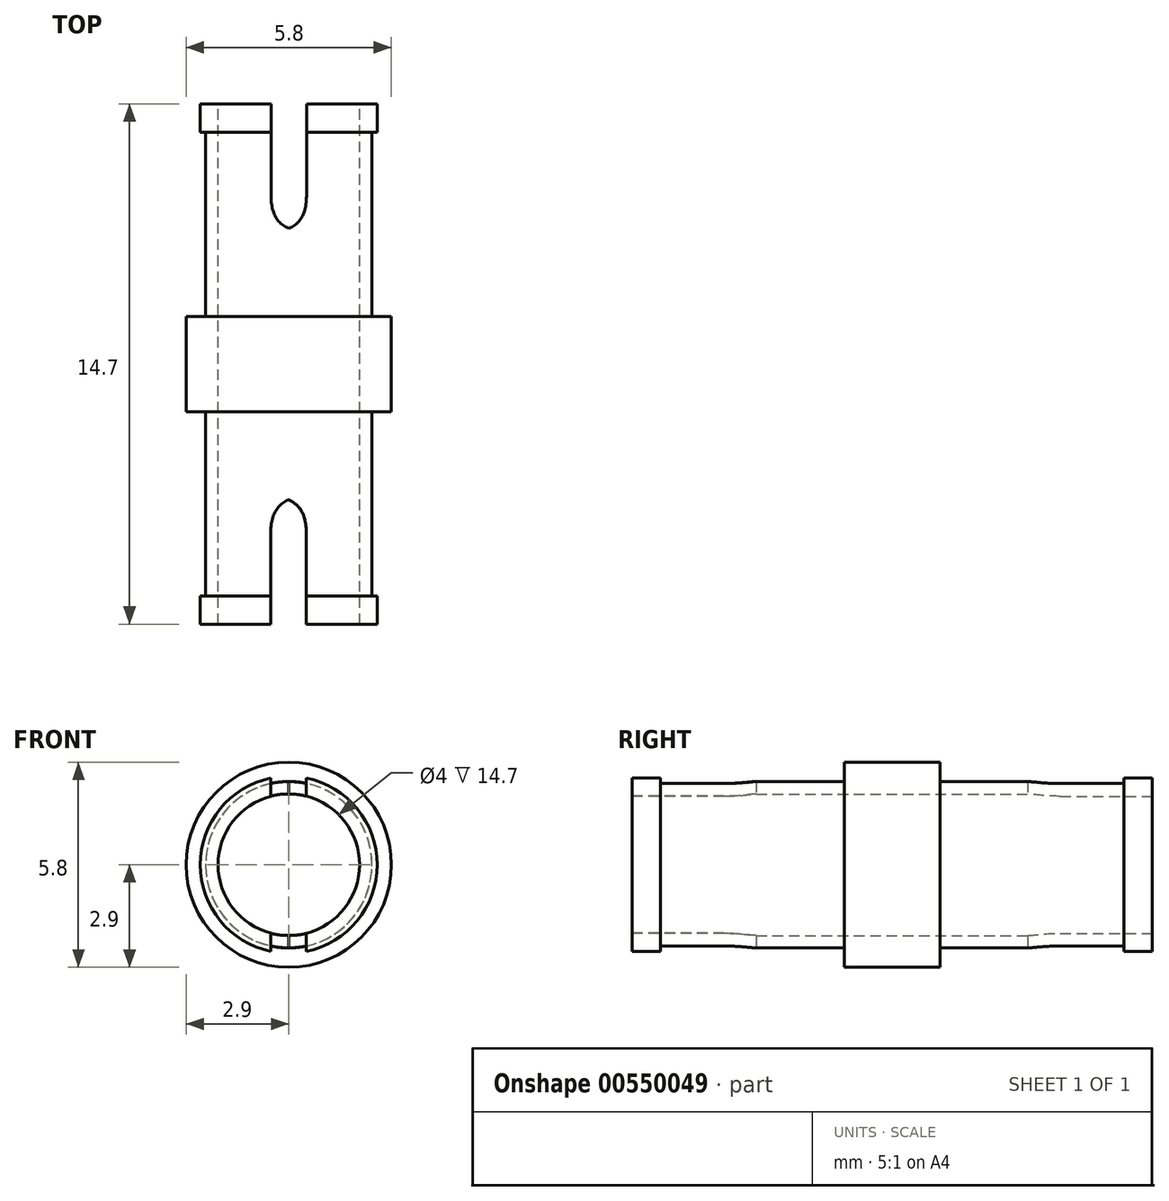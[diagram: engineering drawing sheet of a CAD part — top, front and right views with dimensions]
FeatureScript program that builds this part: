
annotation { "Feature Type Name" : "Feature", "Feature Type Description" : "" }
export const myFeature = defineFeature(function(context is Context, id is Id, definition is map)
    precondition{}
    {
        {
            var Q0;
            Q0=qCreatedBy(makeId("Front.planeOp"),FACE);
            var sketch = newSketch(context, id + "F0", { "sketchPlane" : qUnion([Q0])});
            skCircle(sketch, "E0", {"center": v(0, 0) * mm, "radius": 2.9 * mm});
            skCircle(sketch, "E1", {"center": v(0, 0) * mm, "radius": 2.35 * mm});
            skSolve(sketch);
        }
        {
            var Q0;
            Q0=makeQuery(id+"F0.imprint","IMPRINT",FACE,{"disambiguationData":[TD([[makeQuery(id+"F0.imprint","IMPRINT",EDGE,{"derivedFrom":sQuery(id+"F0.wireOp",EDGE,"E0")}),1.0]])]});
            var Q1;
            Q1=makeQuery(id+"F0.imprint","IMPRINT",FACE,{"disambiguationData":[TD([[makeQuery(id+"F0.imprint","IMPRINT",EDGE,{"derivedFrom":sQuery(id+"F0.wireOp",EDGE,"E1")}),1.0]])]});
            extrude(context, id + "F1", {"entities" : qUnion([Q0, Q1]), "depth" : 2.7 * mm, "offsetDistance" : 25 * mm});
        }
        {
            var Q0;
            Q0=makeQuery(id+"F0.imprint","IMPRINT",FACE,{"disambiguationData":[TD([[makeQuery(id+"F0.imprint","IMPRINT",EDGE,{"derivedFrom":sQuery(id+"F0.wireOp",EDGE,"E1")}),1.0]])]});
            var Q1;
            Q1=sQuery(id+"F0.wireOp",EDGE,"E1");
            extrude(context, id + "F2", {"entities" : qUnion([Q0]), "operationType" : NewBodyOperationType.ADD, "surfaceEntities" : qUnion([Q1]), "oppositeDirection" : true, "depth" : 6 * mm, "offsetDistance" : 25 * mm});
        }
        {
            var Q0;
            Q0=makeQuery(id+"F1.opExtrude","CAP_FACE",FACE,{"disambiguationData":[OSD([sQuery(id+"F0.wireOp",EDGE,"E0")])],"isStart":false});
            var sketch = newSketch(context, id + "F3", { "sketchPlane" : qUnion([Q0])});
            skCircle(sketch, "E2", {"center": v(0, 0) * mm, "radius": 2.35 * mm});
            skSolve(sketch);
        }
        {
            var Q0;
            Q0=makeQuery(id+"F3.imprint","IMPRINT",FACE,{"disambiguationData":[TD([[makeQuery(id+"F3.imprint","IMPRINT",EDGE,{"derivedFrom":sQuery(id+"F3.wireOp",EDGE,"E2")}),1.0]])]});
            var Q1;
            Q1=sQuery(id+"F3.wireOp",EDGE,"E2");
            extrude(context, id + "F4", {"entities" : qUnion([Q0]), "operationType" : NewBodyOperationType.ADD, "surfaceEntities" : qUnion([Q1]), "depth" : 6 * mm, "offsetDistance" : 25 * mm});
        }
        {
            var Q0;
            Q0=makeQuery(id+"F2.opExtrude","CAP_FACE",FACE,{"disambiguationData":[OSD([sQuery(id+"F0.wireOp",EDGE,"E1")])],"isStart":false});
            var sketch = newSketch(context, id + "F5", { "sketchPlane" : qUnion([Q0])});
            skCircle(sketch, "E3", {"center": v(0, 0) * mm, "radius": 2.5 * mm});
            skSolve(sketch);
        }
        {
            var Q0;
            Q0=makeQuery(id+"F5.imprint","IMPRINT",FACE,{"disambiguationData":[TD([[makeQuery(id+"F5.imprint","IMPRINT",EDGE,{"derivedFrom":sQuery(id+"F5.wireOp",EDGE,"E3")}),1.0]])]});
            var Q1;
            Q1=sQuery(id+"F5.wireOp",EDGE,"E3");
            extrude(context, id + "F6", {"entities" : qUnion([Q0]), "operationType" : NewBodyOperationType.ADD, "surfaceEntities" : qUnion([Q1]), "oppositeDirection" : true, "depth" : 0.8 * mm, "offsetDistance" : 25 * mm});
        }
        {
            var Q0;
            Q0=makeQuery(id+"F4.opExtrude","CAP_FACE",FACE,{"disambiguationData":[OSD([sQuery(id+"F3.wireOp",EDGE,"E2")])],"isStart":false});
            var sketch = newSketch(context, id + "F7", { "sketchPlane" : qUnion([Q0])});
            skCircle(sketch, "E4", {"center": v(0, 0) * mm, "radius": 2.5 * mm});
            skSolve(sketch);
        }
        {
            var Q0;
            Q0=makeQuery(id+"F7.imprint","IMPRINT",FACE,{"disambiguationData":[TD([[makeQuery(id+"F7.imprint","IMPRINT",EDGE,{"derivedFrom":sQuery(id+"F7.wireOp",EDGE,"E4")}),1.0]])]});
            var Q1;
            Q1=sQuery(id+"F7.wireOp",EDGE,"E4");
            extrude(context, id + "F8", {"entities" : qUnion([Q0]), "operationType" : NewBodyOperationType.ADD, "surfaceEntities" : qUnion([Q1]), "oppositeDirection" : true, "depth" : 0.8 * mm, "offsetDistance" : 25 * mm});
        }
        {
            var Q0;
            {var subQ0=sQuery(id+"F0.wireOp",EDGE,"E1");Q0=makeQuery(id+"F6.boolean.opBoolean","MERGE",FACE,{"derivedFrom":[makeQuery(id+"F2.opExtrude","CAP_FACE",FACE,{"disambiguationData":[OSD([subQ0])],"isStart":false}),makeQuery(id+"F6.opExtrude","CAP_FACE",FACE,{"disambiguationData":[OSD([subQ0,sQuery(id+"F5.wireOp",EDGE,"E3")])],"isStart":true})]});}
            var sketch = newSketch(context, id + "F9", { "sketchPlane" : qUnion([Q0])});
            skCircle(sketch, "E5", {"center": v(0, 0) * mm, "radius": 2 * mm});
            skSolve(sketch);
        }
        {
            var Q0;
            Q0=makeQuery(id+"F9.imprint","IMPRINT",FACE,{"disambiguationData":[TD([[makeQuery(id+"F9.imprint","IMPRINT",EDGE,{"derivedFrom":sQuery(id+"F9.wireOp",EDGE,"E5")}),1.0]])]});
            var Q1;
            {var subQ0=sQuery(id+"F3.wireOp",EDGE,"E2");Q1=makeQuery(id+"F8.boolean.opBoolean","MERGE",FACE,{"derivedFrom":[makeQuery(id+"F4.opExtrude","CAP_FACE",FACE,{"disambiguationData":[OSD([subQ0])],"isStart":false}),makeQuery(id+"F8.opExtrude","CAP_FACE",FACE,{"disambiguationData":[OSD([subQ0,sQuery(id+"F7.wireOp",EDGE,"E4")])],"isStart":true})]});}
            extrude(context, id + "F10", {"entities" : qUnion([Q0]), "operationType" : NewBodyOperationType.REMOVE, "endBound" : BoundingType.UP_TO_SURFACE, "oppositeDirection" : true, "depth" : 25 * mm, "endBoundEntityFace" : qUnion([Q1]), "offsetDistance" : 25 * mm});
        }
        {
            var Q0;
            {var subQ0=sQuery(id+"F0.wireOp",EDGE,"E1");Q0=makeQuery(id+"F6.boolean.opBoolean","MERGE",FACE,{"derivedFrom":[makeQuery(id+"F2.opExtrude","CAP_FACE",FACE,{"disambiguationData":[OSD([subQ0])],"isStart":false}),makeQuery(id+"F6.opExtrude","CAP_FACE",FACE,{"disambiguationData":[OSD([subQ0,sQuery(id+"F5.wireOp",EDGE,"E3")])],"isStart":true})]});}
            var sketch = newSketch(context, id + "F11", { "sketchPlane" : qUnion([Q0])});
            skLineSegment(sketch, "E6", {"start": v(0.5, 2) * mm, "end": v(0.5, 2.54) * mm});
            skLineSegment(sketch, "E7", {"start": v(0.5, 2.54) * mm, "end": v(-0.5, 2.54) * mm});
            skLineSegment(sketch, "E8", {"start": v(-0.5, 2.54) * mm, "end": v(-0.5, 2) * mm});
            skLineSegment(sketch, "E9", {"start": v(-0.5, 1.82) * mm, "end": v(0.5, 1.82) * mm});
            skLineSegment(sketch, "E10", {"start": v(0.5, 1.82) * mm, "end": v(0.5, 2) * mm});
            skLineSegment(sketch, "E11", {"start": v(-0.5, 2) * mm, "end": v(-0.5, 1.82) * mm});
            skLineSegment(sketch, "E12", {"start": v(-2.5, 0) * mm, "end": v(2.5, 0) * mm});
            skLineSegment(sketch, "E13.MirrorCS", {"start": v(0.5, -2.54) * mm, "end": v(-0.5, -2.54) * mm});
            skLineSegment(sketch, "E14.MirrorCS", {"start": v(0.5, -2) * mm, "end": v(0.5, -2.54) * mm});
            skLineSegment(sketch, "E15.MirrorCS", {"start": v(-0.5, -2.54) * mm, "end": v(-0.5, -2) * mm});
            skLineSegment(sketch, "E16.MirrorCS", {"start": v(-0.5, -1.82) * mm, "end": v(0.5, -1.82) * mm});
            skLineSegment(sketch, "E17.MirrorCS", {"start": v(0.5, -1.82) * mm, "end": v(0.5, -2) * mm});
            skLineSegment(sketch, "E18.MirrorCS", {"start": v(-0.5, -2) * mm, "end": v(-0.5, -1.82) * mm});
            skSolve(sketch);
        }
        {
            var Q0;
            {var subQ0=sQuery(id+"F3.wireOp",EDGE,"E2");Q0=makeQuery(id+"F8.boolean.opBoolean","MERGE",FACE,{"derivedFrom":[makeQuery(id+"F4.opExtrude","CAP_FACE",FACE,{"disambiguationData":[OSD([subQ0])],"isStart":false}),makeQuery(id+"F8.opExtrude","CAP_FACE",FACE,{"disambiguationData":[OSD([subQ0,sQuery(id+"F7.wireOp",EDGE,"E4")])],"isStart":true})]});}
            var sketch = newSketch(context, id + "F12", { "sketchPlane" : qUnion([Q0])});
            skLineSegment(sketch, "E19", {"start": v(0.5, 2) * mm, "end": v(0.5, 2.54) * mm});
            skLineSegment(sketch, "E20", {"start": v(0.5, 2.54) * mm, "end": v(-0.5, 2.54) * mm});
            skLineSegment(sketch, "E21", {"start": v(-0.5, 2.54) * mm, "end": v(-0.5, 2) * mm});
            skLineSegment(sketch, "E22", {"start": v(-0.5, 1.83) * mm, "end": v(0.5, 1.83) * mm});
            skLineSegment(sketch, "E23", {"start": v(0.5, 1.83) * mm, "end": v(0.5, 2) * mm});
            skLineSegment(sketch, "E24", {"start": v(-0.5, 2) * mm, "end": v(-0.5, 1.83) * mm});
            skLineSegment(sketch, "E25", {"start": v(-2.5, 0) * mm, "end": v(2.5, 0) * mm});
            skLineSegment(sketch, "E26.MirrorCS", {"start": v(0.5, -2.53) * mm, "end": v(-0.5, -2.53) * mm});
            skLineSegment(sketch, "E27.MirrorCS", {"start": v(0.5, -2) * mm, "end": v(0.5, -2.53) * mm});
            skLineSegment(sketch, "E28.MirrorCS", {"start": v(-0.5, -2.53) * mm, "end": v(-0.5, -2) * mm});
            skLineSegment(sketch, "E29.MirrorCS", {"start": v(-0.5, -1.81) * mm, "end": v(0.5, -1.81) * mm});
            skLineSegment(sketch, "E30.MirrorCS", {"start": v(0.5, -1.81) * mm, "end": v(0.5, -2) * mm});
            skLineSegment(sketch, "E31.MirrorCS", {"start": v(-0.5, -2) * mm, "end": v(-0.5, -1.81) * mm});
            skSolve(sketch);
        }
        {
            var Q0;
            {var subQ5=sQuery(id+"F11.wireOp",EDGE,"E10");var subQ6=sQuery(id+"F11.wireOp",EDGE,"E6");var subQ7=makeQuery(id+"F11.imprint","INTERSECT",VERTEX,{"derivedFrom":[subQ6,subQ5]});Q0=makeQuery(id+"F11.imprint","IMPRINT",FACE,{"disambiguationData":[TD([[makeQuery(id+"F11.imprint","IMPRINT",EDGE,{"disambiguationData":[TD([[subQ7,-1.0]])],"derivedFrom":subQ6}),1.0]])]});}
            var Q1;
            {var subQ5=sQuery(id+"F11.wireOp",EDGE,"E17.MirrorCS");var subQ6=sQuery(id+"F11.wireOp",EDGE,"E14.MirrorCS");var subQ7=makeQuery(id+"F11.imprint","INTERSECT",VERTEX,{"derivedFrom":[subQ6,subQ5]});Q1=makeQuery(id+"F11.imprint","IMPRINT",FACE,{"disambiguationData":[TD([[makeQuery(id+"F11.imprint","IMPRINT",EDGE,{"disambiguationData":[TD([[subQ7,-1.0]])],"derivedFrom":subQ6}),-1.0]])]});}
            extrude(context, id + "F13", {"entities" : qUnion([Q0, Q1]), "operationType" : NewBodyOperationType.REMOVE, "oppositeDirection" : true, "depth" : 3.6 * mm, "offsetDistance" : 25 * mm});
        }
        {
            var Q0;
            {var subQ7=sQuery(id+"F12.wireOp",EDGE,"E23");var subQ8=sQuery(id+"F12.wireOp",EDGE,"E19");var subQ9=makeQuery(id+"F12.imprint","INTERSECT",VERTEX,{"derivedFrom":[subQ8,subQ7]});Q0=makeQuery(id+"F12.imprint","IMPRINT",FACE,{"disambiguationData":[TD([[makeQuery(id+"F12.imprint","IMPRINT",EDGE,{"disambiguationData":[TD([[subQ9,-1.0]])],"derivedFrom":subQ8}),1.0]])]});}
            var Q1;
            {var subQ7=sQuery(id+"F12.wireOp",EDGE,"E30.MirrorCS");var subQ8=sQuery(id+"F12.wireOp",EDGE,"E27.MirrorCS");var subQ9=makeQuery(id+"F12.imprint","INTERSECT",VERTEX,{"derivedFrom":[subQ8,subQ7]});Q1=makeQuery(id+"F12.imprint","IMPRINT",FACE,{"disambiguationData":[TD([[makeQuery(id+"F12.imprint","IMPRINT",EDGE,{"disambiguationData":[TD([[subQ9,-1.0]])],"derivedFrom":subQ8}),-1.0]])]});}
            extrude(context, id + "F14", {"entities" : qUnion([Q0, Q1]), "operationType" : NewBodyOperationType.REMOVE, "oppositeDirection" : true, "depth" : 3.6 * mm, "offsetDistance" : 25 * mm});
        }
        {
            var Q0;
            Q0=makeQuery(id+"F14.boolean.opBoolean","COPY",EDGE,{"derivedFrom":makeQuery(id+"F14.opExtrude","CAP_EDGE",EDGE,{"disambiguationData":[OSD([sQuery(id+"F12.wireOp",EDGE,"E28.MirrorCS"),sQuery(id+"F12.wireOp",EDGE,"E31.MirrorCS")])],"isStart":false})});
            var Q1;
            Q1=makeQuery(id+"F14.boolean.opBoolean","COPY",EDGE,{"derivedFrom":makeQuery(id+"F14.opExtrude","CAP_EDGE",EDGE,{"disambiguationData":[OSD([sQuery(id+"F12.wireOp",EDGE,"E27.MirrorCS"),sQuery(id+"F12.wireOp",EDGE,"E30.MirrorCS")])],"isStart":false})});
            var Q2;
            Q2=makeQuery(id+"F14.boolean.opBoolean","COPY",EDGE,{"derivedFrom":makeQuery(id+"F14.opExtrude","CAP_EDGE",EDGE,{"disambiguationData":[OSD([sQuery(id+"F12.wireOp",EDGE,"E21"),sQuery(id+"F12.wireOp",EDGE,"E24")])],"isStart":false})});
            var Q3;
            Q3=makeQuery(id+"F14.boolean.opBoolean","COPY",EDGE,{"derivedFrom":makeQuery(id+"F14.opExtrude","CAP_EDGE",EDGE,{"disambiguationData":[OSD([sQuery(id+"F12.wireOp",EDGE,"E19"),sQuery(id+"F12.wireOp",EDGE,"E23")])],"isStart":false})});
            var Q4;
            Q4=makeQuery(id+"F13.boolean.opBoolean","COPY",EDGE,{"derivedFrom":makeQuery(id+"F13.opExtrude","CAP_EDGE",EDGE,{"disambiguationData":[OSD([sQuery(id+"F11.wireOp",EDGE,"E14.MirrorCS"),sQuery(id+"F11.wireOp",EDGE,"E17.MirrorCS")])],"isStart":false})});
            var Q5;
            Q5=makeQuery(id+"F13.boolean.opBoolean","COPY",EDGE,{"derivedFrom":makeQuery(id+"F13.opExtrude","CAP_EDGE",EDGE,{"disambiguationData":[OSD([sQuery(id+"F11.wireOp",EDGE,"E15.MirrorCS"),sQuery(id+"F11.wireOp",EDGE,"E18.MirrorCS")])],"isStart":false})});
            var Q6;
            Q6=makeQuery(id+"F13.boolean.opBoolean","COPY",EDGE,{"derivedFrom":makeQuery(id+"F13.opExtrude","CAP_EDGE",EDGE,{"disambiguationData":[OSD([sQuery(id+"F11.wireOp",EDGE,"E6"),sQuery(id+"F11.wireOp",EDGE,"E10")])],"isStart":false})});
            var Q7;
            Q7=makeQuery(id+"F13.boolean.opBoolean","COPY",EDGE,{"derivedFrom":makeQuery(id+"F13.opExtrude","CAP_EDGE",EDGE,{"disambiguationData":[OSD([sQuery(id+"F11.wireOp",EDGE,"E8"),sQuery(id+"F11.wireOp",EDGE,"E11")])],"isStart":false})});
            fillet(context, id + "F15", {"entities" : qUnion([Q0, Q1, Q2, Q3, Q4, Q5, Q6, Q7]), "radius" : 1 * mm, "rho" : 0.5, "crossSection" : FilletCrossSection.CONIC, "allowEdgeOverflow" : false});
        }
    });
